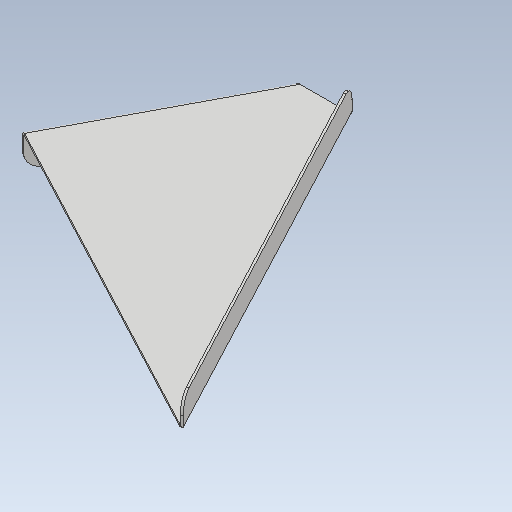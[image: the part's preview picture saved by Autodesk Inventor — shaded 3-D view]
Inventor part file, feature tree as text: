
AUTODESK INVENTOR PART (.ipt)
format: ipt  version: 2020.1 (Build 241239000, 239)  size: 195,072 bytes
history: native  units: mm
features: sheet_metal_op x7, other x4, sketch x3, fillet x1
ambient origin geometry x8: Origin, YZ Plane, XZ Plane, XY Plane, X Axis, Y Axis, Z Axis, Center Point
bodies: Solid1 (feature_tree)
feature tree (15):
  sheet_metal_op  "Face1"
  sheet_metal_op  "Flange1"
  sheet_metal_op  "Flange2"
  fillet  "Fillet1"  Radius=280.0mm
  sketch  "Sketch1"  dims[d2=9.721484mm]
  other  "Plate1"
  sketch  "Sketch2"  dims[d3=3.0mm]
  other  "Plate2"
  sheet_metal_op  "Bend1"
  sheet_metal_op  "Corner1"
  sketch  "Sketch3"  dims[d4=3.0mm d5=1.5mm d6=6.0mm d7=3.75mm d8=46.0mm d9=90.0deg d10=3.75mm d11=12.0mm d12=3.0mm d13=3.75mm d14=535.98483mm d15=80.0mm d16=4.860742mm d17=40.0mm d18=20.0mm d19=3.0mm d20=1.5mm d21=6.0mm d22=3.75mm d23=41.0mm d24=90.0deg d25=3.75mm d26=12.0mm d27=3.0mm d28=3.75mm]
  other  "Plate3"
  sheet_metal_op  "Bend2"
  sheet_metal_op  "Corner2"
  other  "Definition1"
